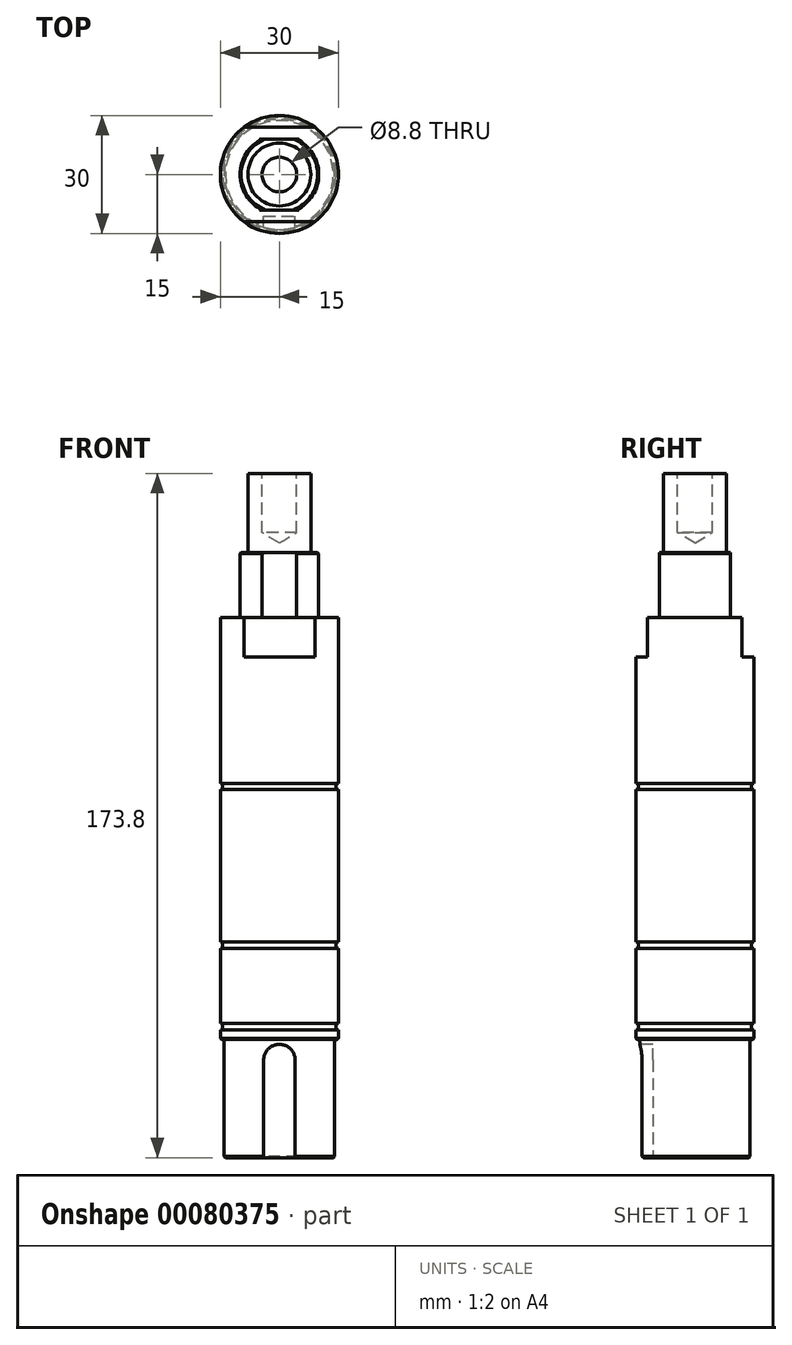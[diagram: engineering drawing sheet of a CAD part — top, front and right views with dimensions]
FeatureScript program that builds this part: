
annotation { "Feature Type Name" : "Feature", "Feature Type Description" : "" }
export const myFeature = defineFeature(function(context is Context, id is Id, definition is map)
    precondition{}
    {
        {
            var Q0;
            Q0=qCreatedBy(makeId("Front.planeOp"),FACE);
            var sketch = newSketch(context, id + "F0", { "sketchPlane" : qUnion([Q0])});
            skLineSegment(sketch, "E0", {"start": v(0, 0) * mm, "end": v(-14, 0) * mm});
            skLineSegment(sketch, "E1", {"start": v(-14, 0) * mm, "end": v(-14, 29.3) * mm});
            skLineSegment(sketch, "E2", {"start": v(-14.7, 30) * mm, "end": v(-15, 30) * mm});
            skLineSegment(sketch, "E3", {"start": v(-15, 30) * mm, "end": v(-15, 32.5) * mm});
            skLineSegment(sketch, "E4", {"start": v(-15, 34.1) * mm, "end": v(-15, 53.2) * mm});
            skLineSegment(sketch, "E5", {"start": v(-15, 53.2) * mm, "end": v(-14.4, 53.2) * mm});
            skLineSegment(sketch, "E6", {"start": v(-14.4, 54.8) * mm, "end": v(-15, 54.8) * mm});
            skLineSegment(sketch, "E7", {"start": v(-15, 54.8) * mm, "end": v(-15, 93.5) * mm});
            skLineSegment(sketch, "E8", {"start": v(-15, 93.5) * mm, "end": v(-14.4, 93.5) * mm});
            skLineSegment(sketch, "E9", {"start": v(-14.4, 95.1) * mm, "end": v(-15, 95.1) * mm});
            skLineSegment(sketch, "E10", {"start": v(-15, 95.1) * mm, "end": v(-15, 137) * mm});
            skLineSegment(sketch, "E11", {"start": v(-15, 136.88) * mm, "end": v(-15, 137.2) * mm});
            skLineSegment(sketch, "E12", {"start": v(-15, 137.2) * mm, "end": v(-10.3, 137.2) * mm});
            skLineSegment(sketch, "E13", {"start": v(-10, 137.5) * mm, "end": v(-10, 153.8) * mm});
            skLineSegment(sketch, "E14", {"start": v(-10, 153.8) * mm, "end": v(-8, 153.8) * mm});
            skLineSegment(sketch, "E15", {"start": v(-8, 153.8) * mm, "end": v(-8, 173.8) * mm});
            skLineSegment(sketch, "E16", {"start": v(-8, 173.8) * mm, "end": v(0, 173.8) * mm});
            skLineSegment(sketch, "E17", {"start": v(0, 173.8) * mm, "end": v(0, 0) * mm});
            skLineSegment(sketch, "E18", {"start": v(-15, 34.1) * mm, "end": v(-14.4, 34.1) * mm});
            skLineSegment(sketch, "E19", {"start": v(-14.4, 34.1) * mm, "end": v(-14.4, 32.5) * mm});
            skLineSegment(sketch, "E20", {"start": v(-14.4, 32.5) * mm, "end": v(-15, 32.5) * mm});
            skLineSegment(sketch, "E21", {"start": v(-14.4, 54.8) * mm, "end": v(-14.4, 53.2) * mm});
            skLineSegment(sketch, "E22", {"start": v(-14.4, 95.1) * mm, "end": v(-14.4, 93.5) * mm});
            skPoint(sketch, "E23.visualSharp", {"position": v(-14, 30) * mm});
            skArc(sketch, "E23.filletArc", {"start": v(-14, 29.3) * mm, "mid": v(-14.2, 29.8) * mm, "end": v(-14.7, 30) * mm});
            skPoint(sketch, "E24.visualSharp", {"position": v(-10, 137.2) * mm});
            skArc(sketch, "E24.filletArc", {"start": v(-10.3, 137.2) * mm, "mid": v(-10.09, 137.29) * mm, "end": v(-10, 137.5) * mm});
            skSolve(sketch);
        }
        {
            var Q0;
            Q0=makeQuery(id+"F0.imprint","IMPRINT",FACE,{"disambiguationData":[TD([[makeQuery(id+"F0.imprint","IMPRINT",EDGE,{"derivedFrom":sQuery(id+"F0.wireOp",EDGE,"E0")}),-1.0]])]});
            var Q1;
            Q1=sQuery(id+"F0.wireOp",EDGE,"E17");
            revolve(context, id + "F1", {"entities" : qUnion([Q0]), "axis" : qUnion([Q1]), "revolveType" : RevolveType.FULL});
        }
        {
            var Q0;
            Q0=makeQuery(id+"F1.opRevolve","SWEPT_EDGE",EDGE,{"disambiguationData":[OSD([sQuery(id+"F0.wireOp",EDGE,"E2"),sQuery(id+"F0.wireOp",EDGE,"E3")])]});
            var Q1;
            Q1=makeQuery(id+"F1.opRevolve","SWEPT_EDGE",EDGE,{"disambiguationData":[OSD([sQuery(id+"F0.wireOp",EDGE,"E13"),sQuery(id+"F0.wireOp",EDGE,"E14")])]});
            var Q2;
            Q2=makeQuery(id+"F1.opRevolve","SWEPT_EDGE",EDGE,{"disambiguationData":[OSD([sQuery(id+"F0.wireOp",EDGE,"E0"),sQuery(id+"F0.wireOp",EDGE,"E1")])]});
            chamfer(context, id + "F2", {"entities" : qUnion([Q0, Q1, Q2]), "width" : .3 * mm, "tangentPropagation" : true});
        }
        {
            var Q0;
            Q0=makeQuery(id+"F1.opRevolve","SWEPT_FACE",FACE,{"disambiguationData":[OSD([sQuery(id+"F0.wireOp",EDGE,"E0")])]});
            var sketch = newSketch(context, id + "F3", { "sketchPlane" : qUnion([Q0])});
            skLineSegment(sketch, "E25", {"start": v(0, 14) * mm, "end": v(0, 10.46) * mm, "construction": true});
            skLineSegment(sketch, "E26", {"start": v(0, 14) * mm, "end": v(0, 15.87) * mm, "construction": true});
            skLineSegment(sketch, "E27", {"start": v(0, 14) * mm, "end": v(-4, 14) * mm});
            skLineSegment(sketch, "E28", {"start": v(-4, 14) * mm, "end": v(-4, 10.6) * mm});
            skLineSegment(sketch, "E29", {"start": v(-4, 10.6) * mm, "end": v(0, 10.6) * mm});
            skLineSegment(sketch, "E30.MirrorCS", {"start": v(0, 14) * mm, "end": v(4, 14) * mm});
            skLineSegment(sketch, "E31.MirrorCS", {"start": v(4, 14) * mm, "end": v(4, 10.6) * mm});
            skLineSegment(sketch, "E32.MirrorCS", {"start": v(4, 10.6) * mm, "end": v(0, 10.6) * mm});
            skSolve(sketch);
        }
        {
            var Q0;
            Q0 = qSketchRegion(id + "F3", true);
            extrude(context, id + "F4", {"entities" : qUnion([Q0]), "operationType" : NewBodyOperationType.REMOVE, "oppositeDirection" : true, "depth" : 28.8 * mm});
        }
        {
            var Q0;
            Q0=makeQuery(id+"F4.boolean.opBoolean","COPY",EDGE,{"derivedFrom":makeQuery(id+"F4.opExtrude","CAP_EDGE",EDGE,{"disambiguationData":[OSD([sQuery(id+"F3.wireOp",EDGE,"E31.MirrorCS")])],"isStart":false})});
            var Q1;
            Q1=makeQuery(id+"F4.boolean.opBoolean","COPY",EDGE,{"derivedFrom":makeQuery(id+"F4.opExtrude","CAP_EDGE",EDGE,{"disambiguationData":[OSD([sQuery(id+"F3.wireOp",EDGE,"E28")])],"isStart":false})});
            fillet(context, id + "F5", {"entities" : qUnion([Q0, Q1]), "radius" : 4 * mm, "tangentPropagation" : true, "allowEdgeOverflow" : false});
        }
        {
            var Q0;
            Q0=makeQuery(id+"F1.opRevolve","SWEPT_FACE",FACE,{"disambiguationData":[OSD([sQuery(id+"F0.wireOp",EDGE,"E14")])]});
            var sketch = newSketch(context, id + "F6", { "sketchPlane" : qUnion([Q0])});
            skLineSegment(sketch, "E33", {"start": v(0, 0) * mm, "end": v(0, -9) * mm, "construction": true});
            skLineSegment(sketch, "E34", {"start": v(0, -9) * mm, "end": v(-16.31, -9) * mm});
            skLineSegment(sketch, "E35", {"start": v(-16.31, -9) * mm, "end": v(-16.31, -10.5) * mm});
            skLineSegment(sketch, "E36", {"start": v(-16.31, -10.5) * mm, "end": v(0, -10.5) * mm});
            skLineSegment(sketch, "E37", {"start": v(0, -10.5) * mm, "end": v(0, -9) * mm});
            skLineSegment(sketch, "E38", {"start": v(0, 0) * mm, "end": v(-3.79, 0) * mm, "construction": true});
            skLineSegment(sketch, "E39.MirrorCS", {"start": v(0, 9) * mm, "end": v(-16.31, 9) * mm});
            skLineSegment(sketch, "E40.MirrorCS", {"start": v(-16.31, 10.5) * mm, "end": v(0, 10.5) * mm});
            skLineSegment(sketch, "E41.MirrorCS", {"start": v(-16.31, 9) * mm, "end": v(-16.31, 10.5) * mm});
            skLineSegment(sketch, "E42.MirrorCS", {"start": v(0, 10.5) * mm, "end": v(0, 9) * mm, "construction": true});
            skLineSegment(sketch, "E43.MirrorCS", {"start": v(16.31, -9) * mm, "end": v(16.31, -10.5) * mm});
            skLineSegment(sketch, "E44.MirrorCS", {"start": v(16.31, -10.5) * mm, "end": v(0, -10.5) * mm});
            skLineSegment(sketch, "E45.MirrorCS", {"start": v(0, -9) * mm, "end": v(16.31, -9) * mm});
            skLineSegment(sketch, "E46.MirrorCS", {"start": v(0, 9) * mm, "end": v(16.31, 9) * mm});
            skLineSegment(sketch, "E47.MirrorCS", {"start": v(16.31, 9) * mm, "end": v(16.31, 10.5) * mm});
            skLineSegment(sketch, "E48.MirrorCS", {"start": v(16.31, 10.5) * mm, "end": v(0, 10.5) * mm});
            skSolve(sketch);
        }
        {
            var Q0;
            Q0 = qSketchRegion(id + "F6", true);
            var Q1;
            Q1=makeQuery(id+"F1.opRevolve","SWEPT_FACE",FACE,{"disambiguationData":[OSD([sQuery(id+"F0.wireOp",EDGE,"E12")])]});
            extrude(context, id + "F7", {"entities" : qUnion([Q0]), "operationType" : NewBodyOperationType.REMOVE, "endBound" : BoundingType.UP_TO_SURFACE, "oppositeDirection" : true, "endBoundEntityFace" : qUnion([Q1]), "depth" : 25 * mm});
        }
        {
            var Q0;
            {var subQ0=sQuery(id+"F0.wireOp",EDGE,"E12");Q0=makeQuery(id+"F7.boolean.opBoolean","MERGE",FACE,{"derivedFrom":[makeQuery(id+"F1.opRevolve","SWEPT_FACE",FACE,{"disambiguationData":[OSD([subQ0])]}),makeQuery(id+"F7.opExtrude","CAP_FACE",FACE,{"disambiguationData":[OSD([subQ0]),ownerDisambiguation([makeQuery(id+"F7.opExtrude","SWEPT_BODY",BODY,{"disambiguationData":[OSD([sQuery(id+"F6.wireOp",EDGE,"E34"),sQuery(id+"F6.wireOp",EDGE,"E35"),sQuery(id+"F6.wireOp",EDGE,"E36"),sQuery(id+"F6.wireOp",EDGE,"E43.MirrorCS"),sQuery(id+"F6.wireOp",EDGE,"E44.MirrorCS"),sQuery(id+"F6.wireOp",EDGE,"E45.MirrorCS")])]})])],"isStart":false}),makeQuery(id+"F7.opExtrude","CAP_FACE",FACE,{"disambiguationData":[OSD([subQ0]),ownerDisambiguation([makeQuery(id+"F7.opExtrude","SWEPT_BODY",BODY,{"disambiguationData":[OSD([sQuery(id+"F6.wireOp",EDGE,"E39.MirrorCS"),sQuery(id+"F6.wireOp",EDGE,"E40.MirrorCS"),sQuery(id+"F6.wireOp",EDGE,"E41.MirrorCS"),sQuery(id+"F6.wireOp",EDGE,"E46.MirrorCS"),sQuery(id+"F6.wireOp",EDGE,"E47.MirrorCS"),sQuery(id+"F6.wireOp",EDGE,"E48.MirrorCS")])]})])],"isStart":false})]});}
            var sketch = newSketch(context, id + "F8", { "sketchPlane" : qUnion([Q0])});
            skLineSegment(sketch, "E49", {"start": v(0, 0) * mm, "end": v(0, 12) * mm});
            skLineSegment(sketch, "E50", {"start": v(0, 12) * mm, "end": v(11.37, 12) * mm});
            skLineSegment(sketch, "E51", {"start": v(11.37, 12) * mm, "end": v(11.37, 17.7) * mm});
            skLineSegment(sketch, "E52", {"start": v(11.37, 17.7) * mm, "end": v(0, 17.7) * mm});
            skLineSegment(sketch, "E53", {"start": v(0, 17.7) * mm, "end": v(0, 12) * mm});
            skLineSegment(sketch, "E54", {"start": v(0, 0) * mm, "end": v(3.33, 0) * mm, "construction": true});
            skLineSegment(sketch, "E55.MirrorCS", {"start": v(11.37, -17.7) * mm, "end": v(0, -17.7) * mm});
            skLineSegment(sketch, "E56.MirrorCS", {"start": v(11.37, -12) * mm, "end": v(11.37, -17.7) * mm});
            skLineSegment(sketch, "E57.MirrorCS", {"start": v(0, -12) * mm, "end": v(11.37, -12) * mm});
            skLineSegment(sketch, "E58.MirrorCS", {"start": v(-11.37, 17.7) * mm, "end": v(0, 17.7) * mm});
            skLineSegment(sketch, "E59.MirrorCS", {"start": v(-11.37, 12) * mm, "end": v(-11.37, 17.7) * mm});
            skLineSegment(sketch, "E60.MirrorCS", {"start": v(0, 12) * mm, "end": v(-11.37, 12) * mm});
            skLineSegment(sketch, "E61.MirrorCS", {"start": v(0, -12) * mm, "end": v(-11.37, -12) * mm});
            skLineSegment(sketch, "E62.MirrorCS", {"start": v(-11.37, -12) * mm, "end": v(-11.37, -17.7) * mm});
            skLineSegment(sketch, "E63.MirrorCS", {"start": v(-11.37, -17.7) * mm, "end": v(0, -17.7) * mm});
            skSolve(sketch);
        }
        {
            var Q0;
            Q0 = qSketchRegion(id + "F8", true);
            extrude(context, id + "F9", {"entities" : qUnion([Q0]), "operationType" : NewBodyOperationType.REMOVE, "oppositeDirection" : true, "depth" : 10 * mm});
        }
        {
            var Q0;
            Q0=makeQuery(id+"F1.opRevolve","SWEPT_FACE",FACE,{"disambiguationData":[OSD([sQuery(id+"F0.wireOp",EDGE,"E16")])]});
            var sketch = newSketch(context, id + "F10", { "sketchPlane" : qUnion([Q0])});
            skPoint(sketch, "E64", {"position": v(0, 0) * mm});
            skSolve(sketch);
        }
        {
            var Q0;
            Q0=sQuery(id+"F10.wireOp",VERTEX,"E64");
            var Q1;
            Q1=makeQuery(id+"F1.opRevolve","SWEPT_BODY",BODY,{"disambiguationData":[OSD([sQuery(id+"F0.wireOp",EDGE,"E0"),sQuery(id+"F0.wireOp",EDGE,"E1"),sQuery(id+"F0.wireOp",EDGE,"E2"),sQuery(id+"F0.wireOp",EDGE,"E3"),sQuery(id+"F0.wireOp",EDGE,"E4"),sQuery(id+"F0.wireOp",EDGE,"E5"),sQuery(id+"F0.wireOp",EDGE,"E6"),sQuery(id+"F0.wireOp",EDGE,"E7"),sQuery(id+"F0.wireOp",EDGE,"E8"),sQuery(id+"F0.wireOp",EDGE,"E9"),sQuery(id+"F0.wireOp",EDGE,"E10"),sQuery(id+"F0.wireOp",EDGE,"E11"),sQuery(id+"F0.wireOp",EDGE,"E12"),sQuery(id+"F0.wireOp",EDGE,"E13"),sQuery(id+"F0.wireOp",EDGE,"E14"),sQuery(id+"F0.wireOp",EDGE,"E15"),sQuery(id+"F0.wireOp",EDGE,"E16"),sQuery(id+"F0.wireOp",EDGE,"E17"),sQuery(id+"F0.wireOp",EDGE,"E18"),sQuery(id+"F0.wireOp",EDGE,"E19"),sQuery(id+"F0.wireOp",EDGE,"E20"),sQuery(id+"F0.wireOp",EDGE,"E21"),sQuery(id+"F0.wireOp",EDGE,"E22"),sQuery(id+"F0.wireOp",EDGE,"E23.filletArc"),sQuery(id+"F0.wireOp",EDGE,"E24.filletArc")])]});
            hole(context, id + "F11", {"style" : HoleStyle.SIMPLE, "endStyle" : HoleEndStyle.BLIND, "standardTappedOrClearance" : lookupTablePath({ "standard" : "ISO", "fit" : "Normal", "size" : "M8", "type" : "Clearance" }), "standardBlindInLast" : lookupTablePath({ "fit" : "Standard", "standard" : "ISO", "size" : "M8", "type" : "Clearance" }), "holeDiameter" : 8.8 * mm, "holeDepth" : 15 * mm, "startFromSketch" : true, "locations" : qUnion([Q0]), "scope" : qUnion([Q1])});
        }
    });
